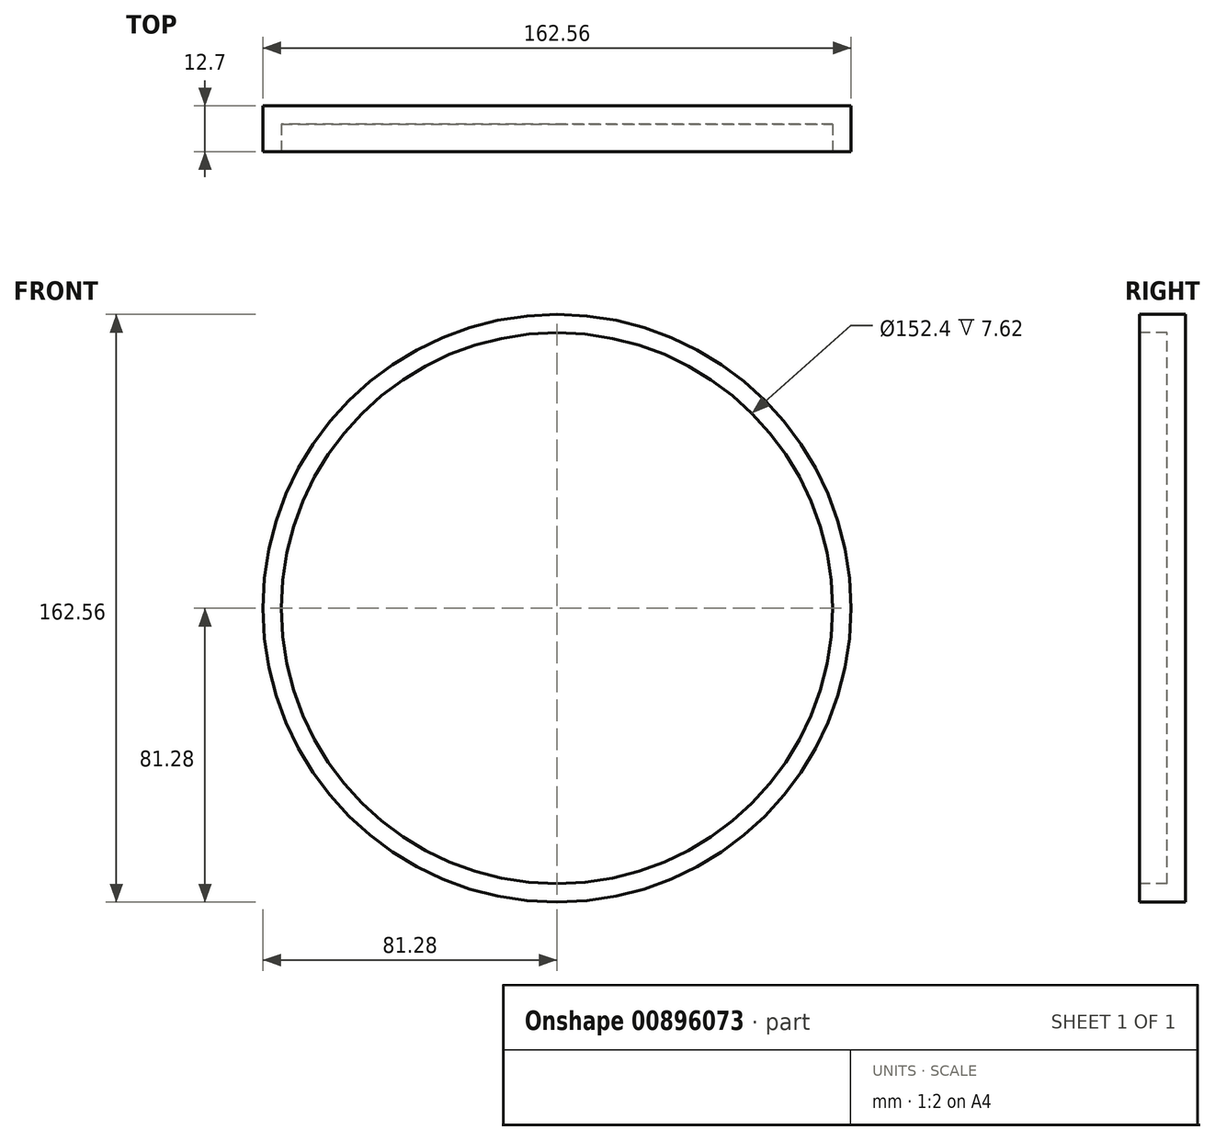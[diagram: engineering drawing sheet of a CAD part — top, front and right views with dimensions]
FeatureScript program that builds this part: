
annotation { "Feature Type Name" : "Feature", "Feature Type Description" : "" }
export const myFeature = defineFeature(function(context is Context, id is Id, definition is map)
    precondition{}
    {
        {
            var Q0;
            Q0=qCreatedBy(makeId("Front.planeOp"),FACE);
            var sketch = newSketch(context, id + "F0", { "sketchPlane" : qUnion([Q0])});
            skCircle(sketch, "E0", {"center": v(0, 0) * mm, "radius": 81.28 * mm});
            skSolve(sketch);
        }
        {
            var Q0;
            Q0=makeQuery(id+"F0.imprint","IMPRINT",FACE,{"disambiguationData":[TD([[makeQuery(id+"F0.imprint","IMPRINT",EDGE,{"derivedFrom":sQuery(id+"F0.wireOp",EDGE,"E0")}),1.0]])]});
            extrude(context, id + "F1", {"entities" : qUnion([Q0]), "depth" : 12.7 * mm, "offsetDistance" : 25.4 * mm});
        }
        {
            var Q0;
            Q0=makeQuery(id+"F1.opExtrude","CAP_FACE",FACE,{"disambiguationData":[OSD([sQuery(id+"F0.wireOp",EDGE,"E0")])],"isStart":false});
            var sketch = newSketch(context, id + "F2", { "sketchPlane" : qUnion([Q0])});
            skCircle(sketch, "E1", {"center": v(0, 0) * mm, "radius": 76.2 * mm});
            skSolve(sketch);
        }
        {
            var Q0;
            Q0=makeQuery(id+"F2.imprint","IMPRINT",FACE,{"disambiguationData":[TD([[makeQuery(id+"F2.imprint","IMPRINT",EDGE,{"derivedFrom":sQuery(id+"F2.wireOp",EDGE,"E1")}),1.0]])]});
            var Q1;
            Q1=makeQuery(id+"F1.opExtrude","CAP_FACE",FACE,{"disambiguationData":[OSD([sQuery(id+"F0.wireOp",EDGE,"E0")])],"isStart":true});
            extrude(context, id + "F3", {"entities" : qUnion([Q0]), "operationType" : NewBodyOperationType.REMOVE, "endBound" : BoundingType.UP_TO_SURFACE, "oppositeDirection" : true, "depth" : 25.4 * mm, "endBoundEntityFace" : qUnion([Q1]), "hasOffset" : true, "offsetDistance" : 5.08 * mm});
        }
    });
